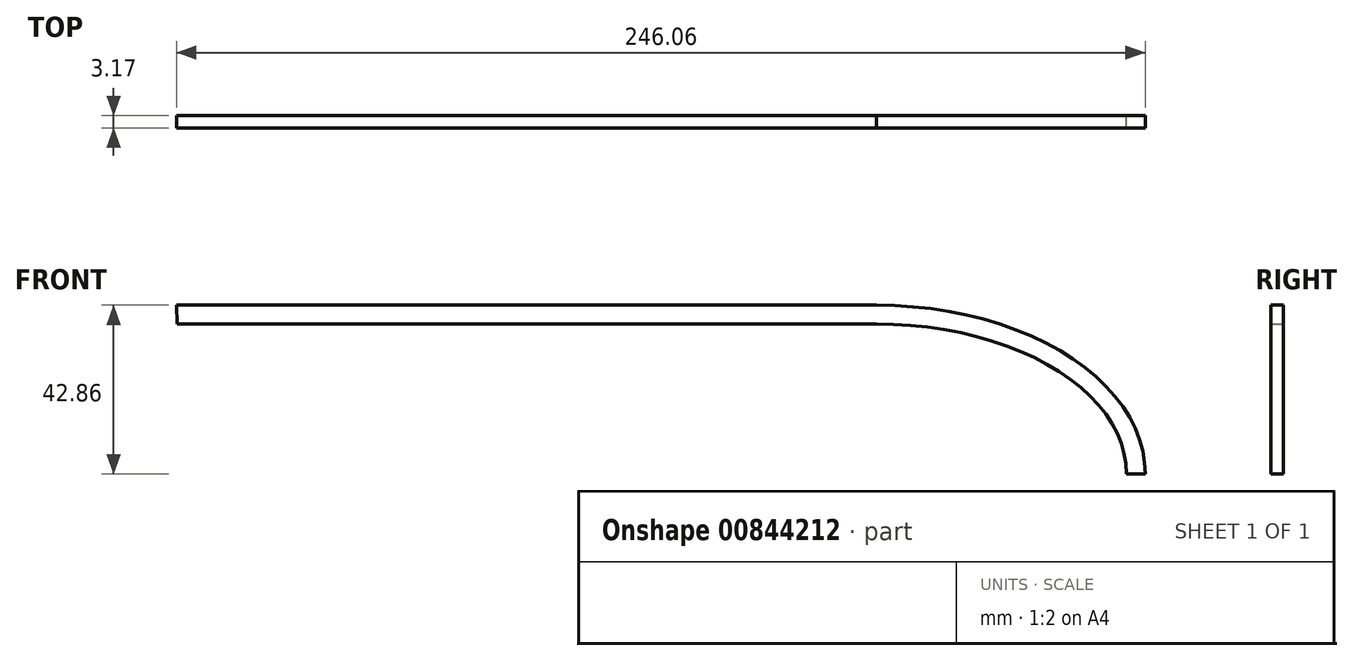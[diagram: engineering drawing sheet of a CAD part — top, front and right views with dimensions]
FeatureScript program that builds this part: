
annotation { "Feature Type Name" : "Feature", "Feature Type Description" : "" }
export const myFeature = defineFeature(function(context is Context, id is Id, definition is map)
    precondition{}
    {
        {
            var Q0;
            Q0=qCreatedBy(makeId("Front.planeOp"),FACE);
            var sketch = newSketch(context, id + "F0", { "sketchPlane" : qUnion([Q0])});
            skLineSegment(sketch, "E0", {"start": v(-55.49, 33.75) * mm, "end": v(122.31, 33.75) * mm});
            skLineSegment(sketch, "E1", {"start": v(-55.49, 33.75) * mm, "end": v(-55.38, 29) * mm});
            skLineSegment(sketch, "E2", {"start": v(-55.38, 29) * mm, "end": v(122.31, 29) * mm});
            skEllipticalArc(sketch, "E3", {});
            skEllipticalArc(sketch, "E4", {});
            skLineSegment(sketch, "E5", {"start": v(122.31, 33.75) * mm, "end": v(122.31, 33.75) * mm});
            skLineSegment(sketch, "E6.trimOffspring", {"start": v(122.31, -47.2) * mm, "end": v(122.31, -51.97) * mm});
            skLineSegment(sketch, "E7", {"start": v(185.81, -9.1) * mm, "end": v(190.57, -9.1) * mm});
            const initialGuessF0  = {"E3": [0.12231225926618779, -0.009109053641145906, 1, 0, 0.0682625, 0.042862500000000005, 0, 1.5707963267948968], "E4": [0.12231225926618779, -0.009109053641145906, 1, 0, 0.0635, 0.0381, 0, 1.5707963267948966]};
            skSetInitialGuess(sketch, initialGuessF0);
            skSolve(sketch);
        }
        {
            var Q0;
            Q0=makeQuery(id+"F0.imprint","IMPRINT",FACE,{"disambiguationData":[TD([[makeQuery(id+"F0.imprint","IMPRINT",EDGE,{"derivedFrom":sQuery(id+"F0.wireOp",EDGE,"E0")}),-1.0]])]});
            extrude(context, id + "F1", {"entities" : qUnion([Q0]), "depth" : 3.17 * mm, "offsetDistance" : 25.4 * mm});
        }
    });
